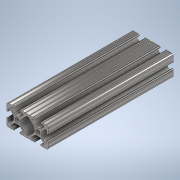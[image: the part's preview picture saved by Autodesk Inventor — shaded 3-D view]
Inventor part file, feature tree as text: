
AUTODESK INVENTOR PART (.ipt)
format: ipt  version: 2020 (Build 240168000, 168)  size: 344,064 bytes
history: native  units: in
note: dims shown in document units (in); Inventor stores cm internally (conversion verified against a paired STEP export)
features: sketch x2, extrude x1
ambient origin geometry x8: Origin, YZ Plane, XZ Plane, XY Plane, X Axis, Y Axis, Z Axis, Center Point
bodies: Solid1 (feature_tree)
feature tree (3):
  extrude  "Extrusion1"  [1 undecoded]
  sketch  "Sketch2"
  sketch  "Sketch1"  dims[d0=6.0in d1=0.0in]
note: 1 required parameter value undecoded (feature->parameter linkage not recoverable at this tier; creation-order binding heuristic only, values carry confidence <= 0.55)
